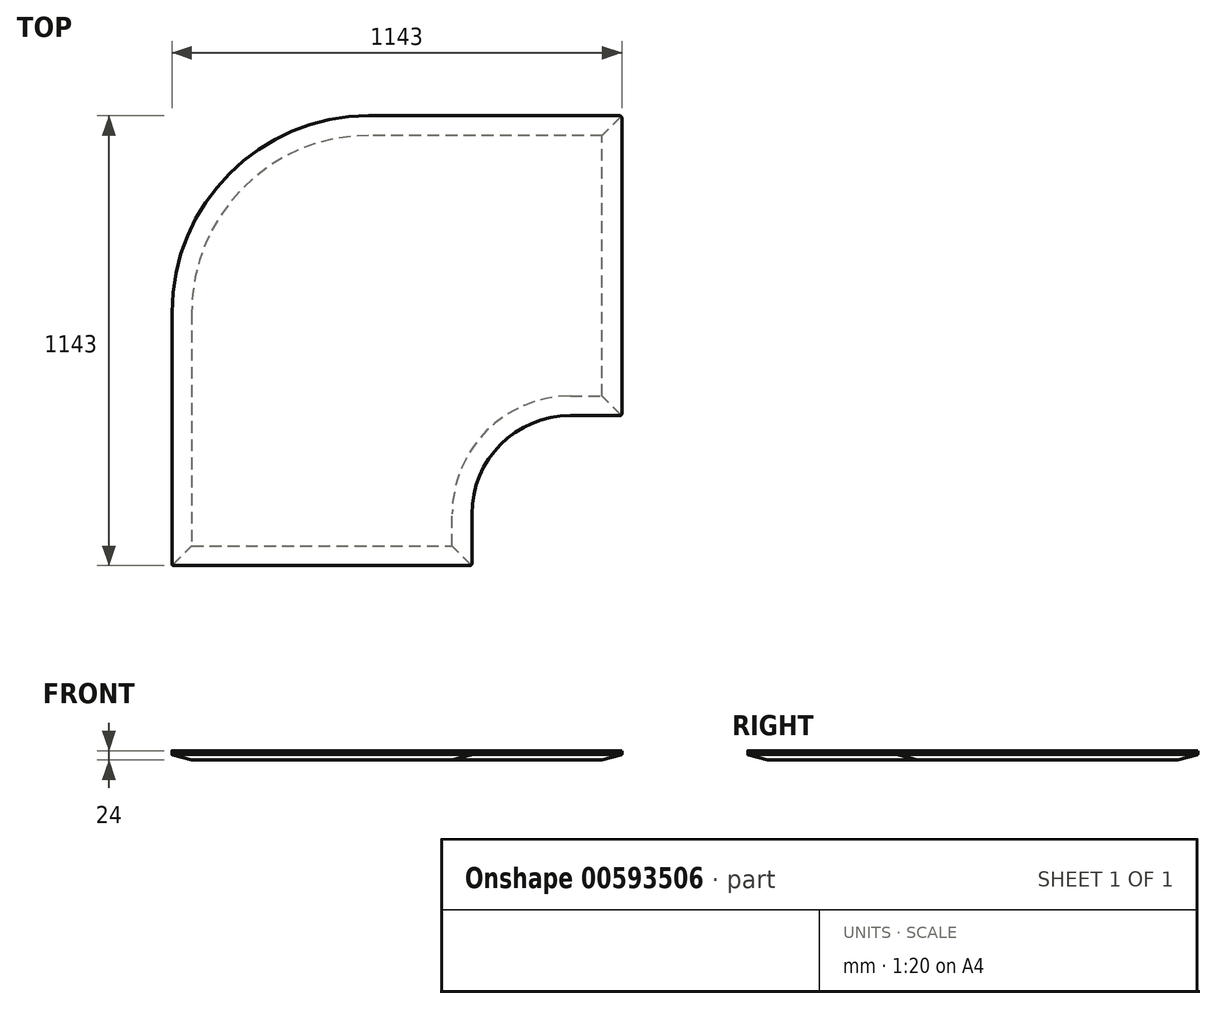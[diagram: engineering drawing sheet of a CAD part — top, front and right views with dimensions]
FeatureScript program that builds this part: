
annotation { "Feature Type Name" : "Feature", "Feature Type Description" : "" }
export const myFeature = defineFeature(function(context is Context, id is Id, definition is map)
    precondition{}
    {
        {
            var Q0;
            Q0=qCreatedBy(makeId("Top.planeOp"),FACE);
            var sketch = newSketch(context, id + "F0", { "sketchPlane" : qUnion([Q0])});
            skLineSegment(sketch, "E0", {"start": v(0, 0) * mm, "end": v(0, 762) * mm});
            skLineSegment(sketch, "E1", {"start": v(0, 762) * mm, "end": v(-643, 762) * mm});
            skLineSegment(sketch, "E2", {"start": v(-1143, 262) * mm, "end": v(-1143, -381) * mm});
            skLineSegment(sketch, "E3", {"start": v(-1143, -381) * mm, "end": v(-381, -381) * mm});
            skLineSegment(sketch, "E4", {"start": v(-1143, 762) * mm, "end": v(-381, 0) * mm, "construction": true});
            skLineSegment(sketch, "E5", {"start": v(-381, -381) * mm, "end": v(-381, -250) * mm});
            skLineSegment(sketch, "E6", {"start": v(-131, 0) * mm, "end": v(0, 0) * mm});
            skPoint(sketch, "E7.visualSharp", {"position": v(-1143, 762) * mm});
            skArc(sketch, "E7.filletArc", {"start": v(-643, 762) * mm, "mid": v(-996.55, 615.55) * mm, "end": v(-1143, 262) * mm});
            skPoint(sketch, "E8.visualSharp", {"position": v(-381, 0) * mm});
            skArc(sketch, "E8.filletArc", {"start": v(-131, 0) * mm, "mid": v(-307.78, -73.22) * mm, "end": v(-381, -250) * mm});
            skSolve(sketch);
        }
        {
            var Q0;
            Q0 = qSketchRegion(id + "F0", true);
            extrude(context, id + "F1", {"entities" : qUnion([Q0]), "depth" : 24 * mm, "offsetDistance" : 25.4 * mm});
        }
        {
            var Q0;
            Q0=makeQuery(id+"F1.opExtrude","SWEPT_FACE",FACE,{"disambiguationData":[OSD([sQuery(id+"F0.wireOp",EDGE,"E0")])]});
            var sketch = newSketch(context, id + "F2", { "sketchPlane" : qUnion([Q0])});
            skLineSegment(sketch, "E9", {"start": v(762, 14) * mm, "end": v(712, 0) * mm});
            skLineSegment(sketch, "E10", {"start": v(712, 0) * mm, "end": v(762, 0) * mm});
            skLineSegment(sketch, "E11", {"start": v(762, 0) * mm, "end": v(762, 14) * mm});
            skSolve(sketch);
        }
        {
            var Q0;
            Q0=makeQuery(id+"F1.opExtrude","CAP_FACE",FACE,{"disambiguationData":[OSD([sQuery(id+"F0.wireOp",EDGE,"E0"),sQuery(id+"F0.wireOp",EDGE,"E1"),sQuery(id+"F0.wireOp",EDGE,"E2"),sQuery(id+"F0.wireOp",EDGE,"E3"),sQuery(id+"F0.wireOp",EDGE,"E5"),sQuery(id+"F0.wireOp",EDGE,"E6"),sQuery(id+"F0.wireOp",EDGE,"E7.filletArc"),sQuery(id+"F0.wireOp",EDGE,"E8.filletArc")])],"isStart":true});
            var sketch = newSketch(context, id + "F3", { "sketchPlane" : qUnion([Q0])});
            skLineSegment(sketch, "E12.0.0", {"start": v(-381, 381) * mm, "end": v(-1143, 381) * mm});
            skLineSegment(sketch, "E12.0.1", {"start": v(-1143, 381) * mm, "end": v(-1143, -262) * mm});
            skArc(sketch, "E12.0.2", {"start": v(-1143, -262) * mm, "mid": v(-996.55, -615.55) * mm, "end": v(-643, -762) * mm});
            skLineSegment(sketch, "E12.0.3", {"start": v(-643, -762) * mm, "end": v(0, -762) * mm});
            skLineSegment(sketch, "E12.0.4", {"start": v(0, -762) * mm, "end": v(0, 0) * mm});
            skLineSegment(sketch, "E12.0.5", {"start": v(0, 0) * mm, "end": v(-131, 0) * mm});
            skArc(sketch, "E12.0.6", {"start": v(-131, 0) * mm, "mid": v(-307.78, 73.22) * mm, "end": v(-381, 250) * mm});
            skLineSegment(sketch, "E12.0.7", {"start": v(-381, 250) * mm, "end": v(-381, 381) * mm});
            skSolve(sketch);
        }
        {
            var Q0;
            Q0=makeQuery(id+"F2.imprint","IMPRINT",FACE,{"disambiguationData":[TD([[makeQuery(id+"F2.imprint","IMPRINT",EDGE,{"derivedFrom":sQuery(id+"F2.wireOp",EDGE,"E9")}),1.0]])]});
            var Q1;
            Q1 = qConstructionFilter(qBodyType(qCreatedBy(id + "F3" ,EDGE), BodyType.WIRE), ConstructionObject.NO);
            sweep(context, id + "F4", {"operationType" : NewBodyOperationType.REMOVE, "profiles" : qUnion([Q0]), "path" : qUnion([Q1])});
        }
        {
            var Q0;
            Q0=makeQuery(id+"F1.opExtrude","SWEPT_EDGE",EDGE,{"disambiguationData":[OSD([sQuery(id+"F0.wireOp",EDGE,"E0"),sQuery(id+"F0.wireOp",EDGE,"E1")])]});
            var Q1;
            Q1=makeQuery(id+"F1.opExtrude","SWEPT_EDGE",EDGE,{"disambiguationData":[OSD([sQuery(id+"F0.wireOp",EDGE,"E0"),sQuery(id+"F0.wireOp",EDGE,"E6")])]});
            var Q2;
            Q2=makeQuery(id+"F1.opExtrude","SWEPT_EDGE",EDGE,{"disambiguationData":[OSD([sQuery(id+"F0.wireOp",EDGE,"E3"),sQuery(id+"F0.wireOp",EDGE,"E5")])]});
            var Q3;
            Q3=makeQuery(id+"F1.opExtrude","SWEPT_EDGE",EDGE,{"disambiguationData":[OSD([sQuery(id+"F0.wireOp",EDGE,"E2"),sQuery(id+"F0.wireOp",EDGE,"E3")])]});
            fillet(context, id + "F5", {"entities" : qUnion([Q0, Q1, Q2, Q3]), "radius" : 5.08 * mm, "tangentPropagation" : true, "allowEdgeOverflow" : false});
        }
    });
